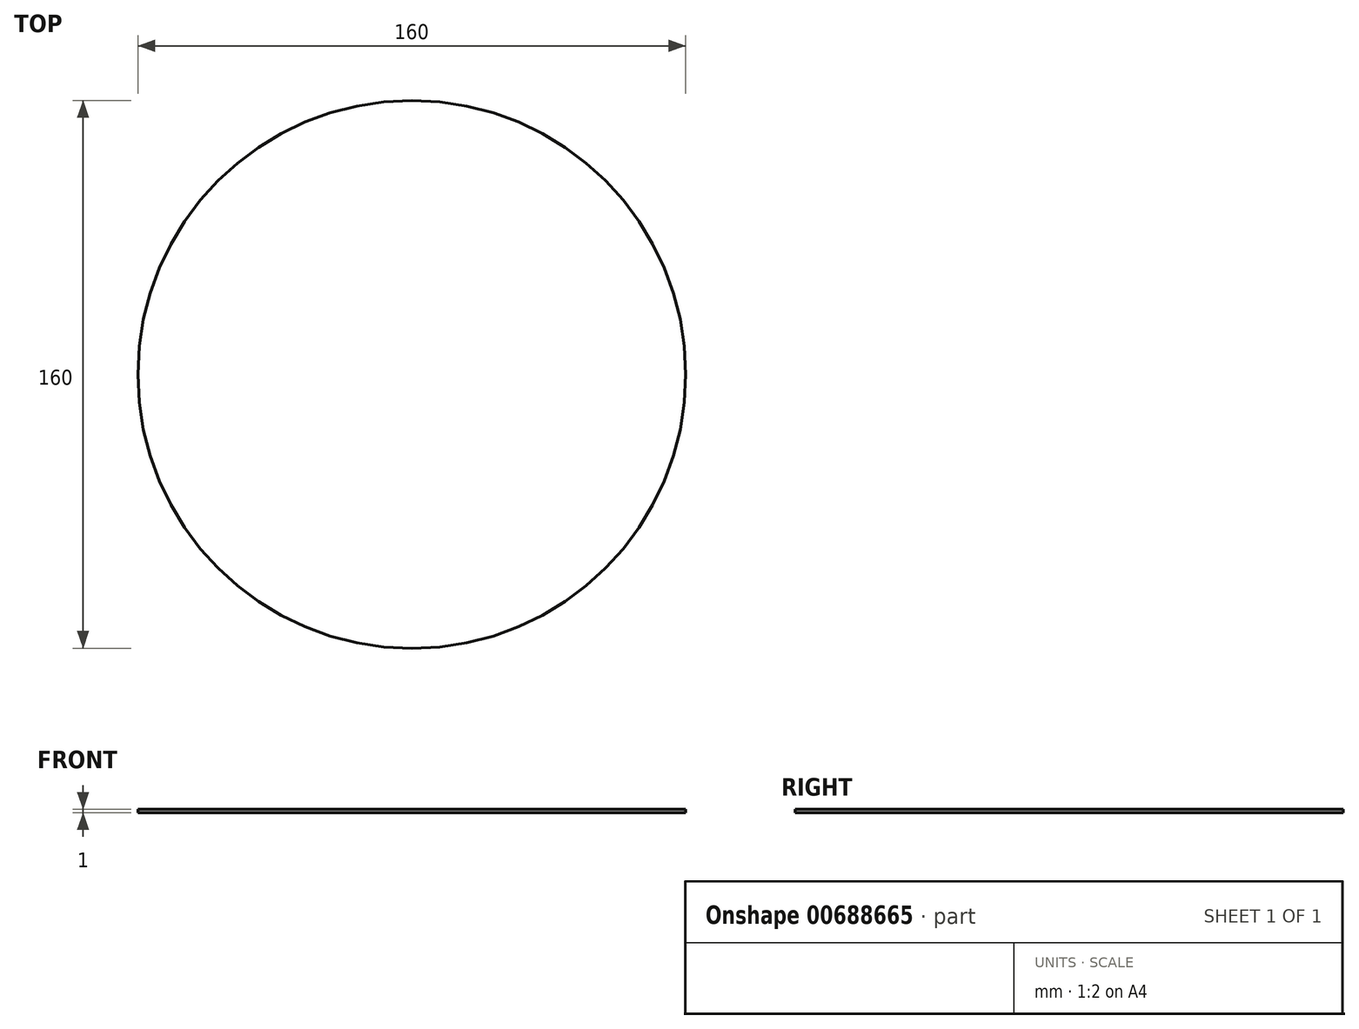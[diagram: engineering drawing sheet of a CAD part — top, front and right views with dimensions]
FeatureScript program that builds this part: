
annotation { "Feature Type Name" : "Feature", "Feature Type Description" : "" }
export const myFeature = defineFeature(function(context is Context, id is Id, definition is map)
    precondition{}
    {
        {
            var Q0;
            Q0=qCreatedBy(makeId("Top.planeOp"),FACE);
            var sketch = newSketch(context, id + "F0", { "sketchPlane" : qUnion([Q0])});
            skCircle(sketch, "E0", {"center": v(0, 0) * mm, "radius": 80 * mm});
            skSolve(sketch);
        }
        {
            var Q0;
            Q0 = qSketchRegion(id + "F0", true);
            var Q1;
            Q1=sQuery(id+"F0.wireOp",EDGE,"960bf385-3883-4e7f-9558-3aba6d1c32c9.right");
            var Q2;
            Q2=sQuery(id+"F0.wireOp",EDGE,"960bf385-3883-4e7f-9558-3aba6d1c32c9.top");
            var Q3;
            Q3=sQuery(id+"F0.wireOp",EDGE,"960bf385-3883-4e7f-9558-3aba6d1c32c9.left");
            var Q4;
            Q4=sQuery(id+"F0.wireOp",EDGE,"960bf385-3883-4e7f-9558-3aba6d1c32c9.bottom");
            extrude(context, id + "F1", {"entities" : qUnion([Q0]), "surfaceEntities" : qUnion([Q1, Q2, Q3, Q4]), "depth" : 1 * mm, "offsetDistance" : 25 * mm});
        }
    });
